FCSTD DOCUMENT  (FreeCAD 0.16R)
Label: Frames
License: All rights reserved
LicenseURL: http://en.wikipedia.org/wiki/All_rights_reserved
objects: Sketcher::SketchObject×1
note: 1 computed .brp shape members not serialized (recipe doc carries the construction recipe); baked Part::Feature solids carry a one-line shape summary decoded from their .brp

FEATURE [Sketcher::SketchObject] Sketch
  sketch-geometry (26):
    g0: LineSegment StartX=-177.09 StartY=413.899 StartZ=0 EndX=-144.415 EndY=426.441 EndZ=0
    g1: LineSegment StartX=-144.415 StartY=426.441 StartZ=0 EndX=-108.578 EndY=333.083 EndZ=0
    g2: LineSegment StartX=-108.578 StartY=333.083 StartZ=0 EndX=-141.253 EndY=320.541 EndZ=0
    g3: LineSegment StartX=-141.253 StartY=320.541 StartZ=0 EndX=-177.09 EndY=413.899 EndZ=0
    g4: LineSegment StartX=-881.016 StartY=5.42606 StartZ=0 EndX=-538.009 EndY=-7.8858 EndZ=0
    g5: LineSegment StartX=-889.831 StartY=14.0812 StartZ=0 EndX=-594.513 EndY=197.031 EndZ=0
    g6: LineSegment StartX=-600.371 StartY=216.19 StartZ=0 EndX=-534.524 EndY=0.81304 EndZ=0
    g7: LineSegment StartX=-572.891 StartY=224.129 StartZ=0 EndX=-502.92 EndY=-4.73728 EndZ=0
    g8: LineSegment StartX=-563.13 StartY=192.2 StartZ=0 EndX=-170.449 EndY=396.599 EndZ=0
    g9: LineSegment StartX=-555.577 StartY=167.496 StartZ=0 EndX=-161.288 EndY=372.732 EndZ=0
    g10: LineSegment StartX=-156.997 StartY=361.555 StartZ=0 EndX=-537.239 EndY=-15.6042 EndZ=0
    g11: LineSegment StartX=-147.051 StartY=335.645 StartZ=0 EndX=-504.48 EndY=-18.887 EndZ=0
    g12: LineSegment StartX=-881.016 StartY=5.42606 StartZ=0 EndX=-590.885 EndY=185.163 EndZ=0
    g13: LineSegment StartX=-881.512 StartY=-6.5637 StartZ=0 EndX=-535.095 EndY=-20.0079 EndZ=0
    g14: Circle CenterX=-520.133 CenterY=-10 CenterZ=0 NormalX=0 NormalY=0 NormalZ=1 Radius=18
    g15: Circle CenterX=-895 CenterY=0 CenterZ=0 NormalX=0 NormalY=0 NormalZ=1 Radius=15
    g16: LineSegment StartX=-134.252 StartY=323.228 StartZ=0 EndX=-8.86901 EndY=-3.4045 EndZ=0
    g17: Circle CenterX=0 CenterY=0 CenterZ=0 NormalX=0 NormalY=0 NormalZ=1 Radius=15
    g18: LineSegment StartX=8.86901 StartY=3.4045 StartZ=0 EndX=-116.514 EndY=330.037 EndZ=0
    g19: LineSegment StartX=-600.371 StartY=216.19 StartZ=0 EndX=-572.891 EndY=224.129 EndZ=0
    g20: LineSegment StartX=8.86901 StartY=3.4045 StartZ=0 EndX=-8.86901 EndY=-3.4045 EndZ=0
    g21: Circle CenterX=-895 CenterY=0 CenterZ=0 NormalX=0 NormalY=0 NormalZ=1 Radius=254
    g22: Circle CenterX=0 CenterY=0 CenterZ=0 NormalX=0 NormalY=0 NormalZ=1 Radius=254
    g23: LineSegment StartX=-202.393 StartY=528.648 StartZ=0 EndX=98.037 EndY=-254 EndZ=0
    g24: LineSegment StartX=374.437 StartY=-254 StartZ=0 EndX=-993.121 EndY=-254 EndZ=0
    g25: Circle CenterX=-520.133 CenterY=-10 CenterZ=0 NormalX=0 NormalY=0 NormalZ=1 Radius=120
  constraints (74):
    c: Coincident(g0,g1)
    c: Coincident(g1,g2)
    c: Coincident(g2,g3)
    c: Coincident(g3,g0)
    c: Distance(g1) = 100
    c: Distance(g2) = 35
    c: Equal(g1,g3)
    c: Perpendicular(g3,g0)
    c: Equal(g2,g0)
    c: Angle(g1) = -1.20428
    c: Parallel(g7,g6)
    c: DistanceY(g14) = -10
    c: PointOnObject(g15,g-1)
    c: DistanceX(g15) = -895
    c: Radius(g14) = 18
    c: PointOnObject(g4,g14)
    c: Radius(g15) = 15
    c: PointOnObject(g4,g15)
    c: Parallel(g13,g4)
    c: Distance(g13,g4) = 12
    c: PointOnObject(g13,g14)
    c: PointOnObject(g13,g15)
    c: Distance(g15,g14) = 375
    c: Parallel(g11,g10)
    c: Parallel(g9,g8)
    c: Parallel(g5,g12)
    c: Distance(g5,g12) = 12
    c: Distance(g9,g8) = 25.4
    c: Distance(g11,g10) = 25.4
    c: PointOnObject(g11,g14)
    c: PointOnObject(g10,g14)
    c: PointOnObject(g11,g3)
    c: PointOnObject(g10,g3)
    c: PointOnObject(g9,g3)
    c: PointOnObject(g8,g3)
    c: PointOnObject(g7,g14)
    c: Distance(g7,g6) = 28.6
    c: Angle(g7) = -1.27409
    c: PointOnObject(g8,g7)
    c: PointOnObject(g9,g7)
    c: PointOnObject(g5,g6)
    c: PointOnObject(g12,g6)
    c: PointOnObject(g5,g15)
    c: PointOnObject(g12,g15)
    c: Distance(g14,g6) = 240
    c: Distance(g7,g14) = 240
    c: PointOnObject(g6,g14)
    c: PointOnObject(g16,g2)
    c: Coincident(g17,g-1)
    c: Radius(g17) = 15
    c: Parallel(g18,g16)
    c: Distance(g18,g16) = 19
    c: Angle(g16) = -1.20428
    c: PointOnObject(g18,g2)
    c: Distance(g-1,g16) = 350
    c: Distance(g16,g2) = 7.5
    c: Symmetric(g18,g16,g-1)
    c: Coincident(g19,g7)
    c: Coincident(g19,g6)
    c: Coincident(g20,g18)
    c: Coincident(g20,g16)
    c: Perpendicular(g18,g20)
    c: Radius(g21) = 254
    c: Coincident(g21,g15)
    c: Coincident(g4,g12)
    c: Coincident(g22,g-1)
    c: Radius(g22) = 254
    c: Parallel(g23,g18)
    c: Symmetric(g0,g0,g23)
    c: Horizontal(g24)
    c: Tangent(g21,g24)
    c: PointOnObject(g23,g24)
    c: Radius(g25) = 120
    c: Coincident(g25,g14)
